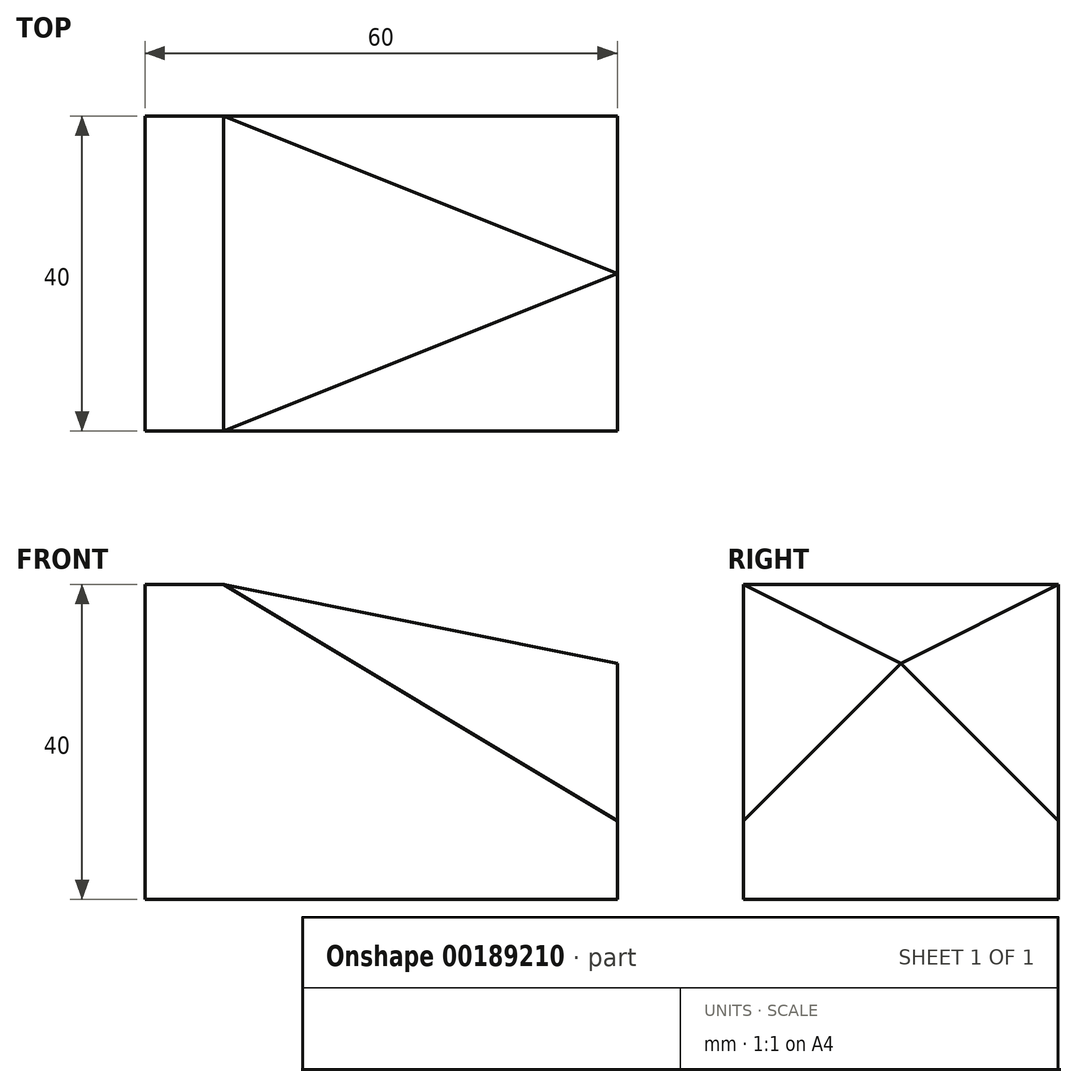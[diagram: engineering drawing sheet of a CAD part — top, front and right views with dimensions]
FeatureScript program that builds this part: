
annotation { "Feature Type Name" : "Feature", "Feature Type Description" : "" }
export const myFeature = defineFeature(function(context is Context, id is Id, definition is map)
    precondition{}
    {
        {
            var Q0;
            Q0=qCreatedBy(makeId("Top.planeOp"),FACE);
            var sketch = newSketch(context, id + "F0", { "sketchPlane" : qUnion([Q0])});
            skLineSegment(sketch, "E0.bottom", {"start": v(0, 0) * mm, "end": v(60, 0) * mm});
            skLineSegment(sketch, "E0.top", {"start": v(0, 40) * mm, "end": v(60, 40) * mm});
            skLineSegment(sketch, "E0.left", {"start": v(0, 0) * mm, "end": v(0, 40) * mm});
            skLineSegment(sketch, "E0.right", {"start": v(60, 0) * mm, "end": v(60, 40) * mm});
            skSolve(sketch);
        }
        {
            var Q0;
            Q0=makeQuery(id+"F0.imprint","IMPRINT",FACE,{"disambiguationData":[TD([[makeQuery(id+"F0.imprint","IMPRINT",EDGE,{"derivedFrom":sQuery(id+"F0.wireOp",EDGE,"E0.bottom")}),1.0]])]});
            extrude(context, id + "F1", {"entities" : qUnion([Q0]), "depth" : 40 * mm});
        }
        {
            var Q0;
            Q0=makeQuery(id+"F1.opExtrude","CAP_EDGE",EDGE,{"disambiguationData":[OSD([sQuery(id+"F0.wireOp",EDGE,"E0.right")])],"isStart":false});
            chamfer(context, id + "F2", {"entities" : qUnion([Q0]), "chamferType" : ChamferType.TWO_OFFSETS, "width1" : 50 * mm, "oppositeDirection" : false, "width2" : 10 * mm, "tangentPropagation" : true});
        }
        {
            var Q0;
            Q0=makeQuery(id+"F1.opExtrude","SWEPT_FACE",FACE,{"disambiguationData":[OSD([sQuery(id+"F0.wireOp",EDGE,"E0.bottom")])]});
            var sketch = newSketch(context, id + "F3", { "sketchPlane" : qUnion([Q0])});
            skPoint(sketch, "E1", {"position": v(60, 10) * mm});
            skSolve(sketch);
        }
        {
            var Q0;
            {var subQ0=sQuery(id+"F0.wireOp",EDGE,"E0.right");Q0=makeQuery(id+"F2.opChamfer","BLEND_EDGE",EDGE,{"blendedFrom":[makeQuery(id+"F1.opExtrude","CAP_EDGE",EDGE,{"disambiguationData":[OSD([subQ0])],"isStart":false}),makeQuery(id+"F1.opExtrude","SWEPT_FACE",FACE,{"disambiguationData":[OSD([subQ0])]})],"blendedInto":[makeQuery(id+"F1.opExtrude","SWEPT_FACE",FACE,{"disambiguationData":[OSD([subQ0])]})]});}
            cPoint(context, id + "F4", {"entities" : qUnion([Q0]), "parameter" : 0.5});
        }
        {
            var Q0;
            {var subQ0=sQuery(id+"F0.wireOp",EDGE,"E0.right");var subQ1=sQuery(id+"F0.wireOp",EDGE,"E0.bottom");Q0=makeQuery(id+"F2.opChamfer","BLEND_VERTEX",VERTEX,{"blendedFrom":[makeQuery(id+"F1.opExtrude","CAP_EDGE",EDGE,{"disambiguationData":[OSD([subQ0])],"isStart":false}),makeQuery(id+"F1.opExtrude","SWEPT_FACE",FACE,{"disambiguationData":[OSD([subQ1])]}),makeQuery(id+"F1.opExtrude","CAP_FACE",FACE,{"disambiguationData":[OSD([subQ1,sQuery(id+"F0.wireOp",EDGE,"E0.top"),sQuery(id+"F0.wireOp",EDGE,"E0.left"),subQ0])],"isStart":false})],"blendedInto":[makeQuery(id+"F1.opExtrude","SWEPT_FACE",FACE,{"disambiguationData":[OSD([subQ1])]}),makeQuery(id+"F1.opExtrude","CAP_FACE",FACE,{"disambiguationData":[OSD([subQ1,sQuery(id+"F0.wireOp",EDGE,"E0.top"),sQuery(id+"F0.wireOp",EDGE,"E0.left"),subQ0])],"isStart":false})]});}
            var Q1;
            Q1 = qCreatedBy(id + "F4" ,VERTEX);
            var Q2;
            Q2=sQuery(id+"F3.wireOp",VERTEX,"E1");
            cPlane(context, id + "F5", {"entities" : qUnion([Q0, Q1, Q2]), "cplaneType" : CPlaneType.THREE_POINT, "offset" : 25 * mm, "width" : 150 * mm, "height" : 150 * mm});
        }
        {
            var Q0;
            Q0=qCreatedBy(id+"F5.planeOp",FACE);
            var sketch = newSketch(context, id + "F6", { "sketchPlane" : qUnion([Q0])});
            skLineSegment(sketch, "E2", {"start": v(-1.84, 28.28) * mm, "end": v(52.47, 35.36) * mm});
            skLineSegment(sketch, "E3", {"start": v(52.47, 35.36) * mm, "end": v(52.47, 7.07) * mm});
            skLineSegment(sketch, "E4", {"start": v(52.47, 7.07) * mm, "end": v(-1.84, 28.28) * mm});
            skSolve(sketch);
        }
        {
            var Q0;
            Q0 = qSketchRegion(id + "F6", true);
            extrude(context, id + "F7", {"entities" : qUnion([Q0]), "operationType" : NewBodyOperationType.REMOVE, "endBound" : BoundingType.THROUGH_ALL, "depth" : 25 * mm});
        }
        {
            var Q0;
            Q0=makeQuery(id+"F1.opExtrude","SWEPT_FACE",FACE,{"disambiguationData":[OSD([sQuery(id+"F0.wireOp",EDGE,"E0.top")])]});
            var sketch = newSketch(context, id + "F8", { "sketchPlane" : qUnion([Q0])});
            skPoint(sketch, "E5", {"position": v(-60, 10) * mm});
            skSolve(sketch);
        }
        {
            var Q0;
            {var subQ0=sQuery(id+"F0.wireOp",EDGE,"E0.top");var subQ1=sQuery(id+"F0.wireOp",EDGE,"E0.right");Q0=makeQuery(id+"F2.opChamfer","BLEND_VERTEX",VERTEX,{"blendedFrom":[makeQuery(id+"F1.opExtrude","CAP_EDGE",EDGE,{"disambiguationData":[OSD([subQ1])],"isStart":false}),makeQuery(id+"F1.opExtrude","CAP_FACE",FACE,{"disambiguationData":[OSD([sQuery(id+"F0.wireOp",EDGE,"E0.bottom"),subQ0,sQuery(id+"F0.wireOp",EDGE,"E0.left"),subQ1])],"isStart":false}),makeQuery(id+"F1.opExtrude","SWEPT_FACE",FACE,{"disambiguationData":[OSD([subQ0])]})],"blendedInto":[makeQuery(id+"F1.opExtrude","CAP_FACE",FACE,{"disambiguationData":[OSD([sQuery(id+"F0.wireOp",EDGE,"E0.bottom"),subQ0,sQuery(id+"F0.wireOp",EDGE,"E0.left"),subQ1])],"isStart":false}),makeQuery(id+"F1.opExtrude","SWEPT_FACE",FACE,{"disambiguationData":[OSD([subQ0])]})]});}
            var Q1;
            Q1=makeQuery(id+"F7.boolean.opBoolean","COPY",VERTEX,{"derivedFrom":makeQuery(id+"F7.opExtrude","CAP_VERTEX",VERTEX,{"disambiguationData":[OSD([sQuery(id+"F6.wireOp",EDGE,"E2"),sQuery(id+"F6.wireOp",EDGE,"E3")])],"isStart":true})});
            var Q2;
            Q2=sQuery(id+"F8.wireOp",VERTEX,"E5");
            cPlane(context, id + "F9", {"entities" : qUnion([Q0, Q1, Q2]), "cplaneType" : CPlaneType.THREE_POINT, "offset" : 25 * mm, "width" : 150 * mm, "height" : 150 * mm});
        }
        {
            var Q0;
            Q0=qCreatedBy(id+"F9.planeOp",FACE);
            var sketch = newSketch(context, id + "F10", { "sketchPlane" : qUnion([Q0])});
            skLineSegment(sketch, "E6", {"start": v(-12.89, 0) * mm, "end": v(41.43, -21.21) * mm});
            skLineSegment(sketch, "E7", {"start": v(41.43, -21.21) * mm, "end": v(41.43, 7.07) * mm});
            skLineSegment(sketch, "E8", {"start": v(41.43, 7.07) * mm, "end": v(-12.89, 0) * mm});
            skSolve(sketch);
        }
        {
            var Q0;
            Q0 = qSketchRegion(id + "F10", true);
            extrude(context, id + "F11", {"entities" : qUnion([Q0]), "operationType" : NewBodyOperationType.REMOVE, "endBound" : BoundingType.THROUGH_ALL, "oppositeDirection" : true, "depth" : 25 * mm});
        }
    });
